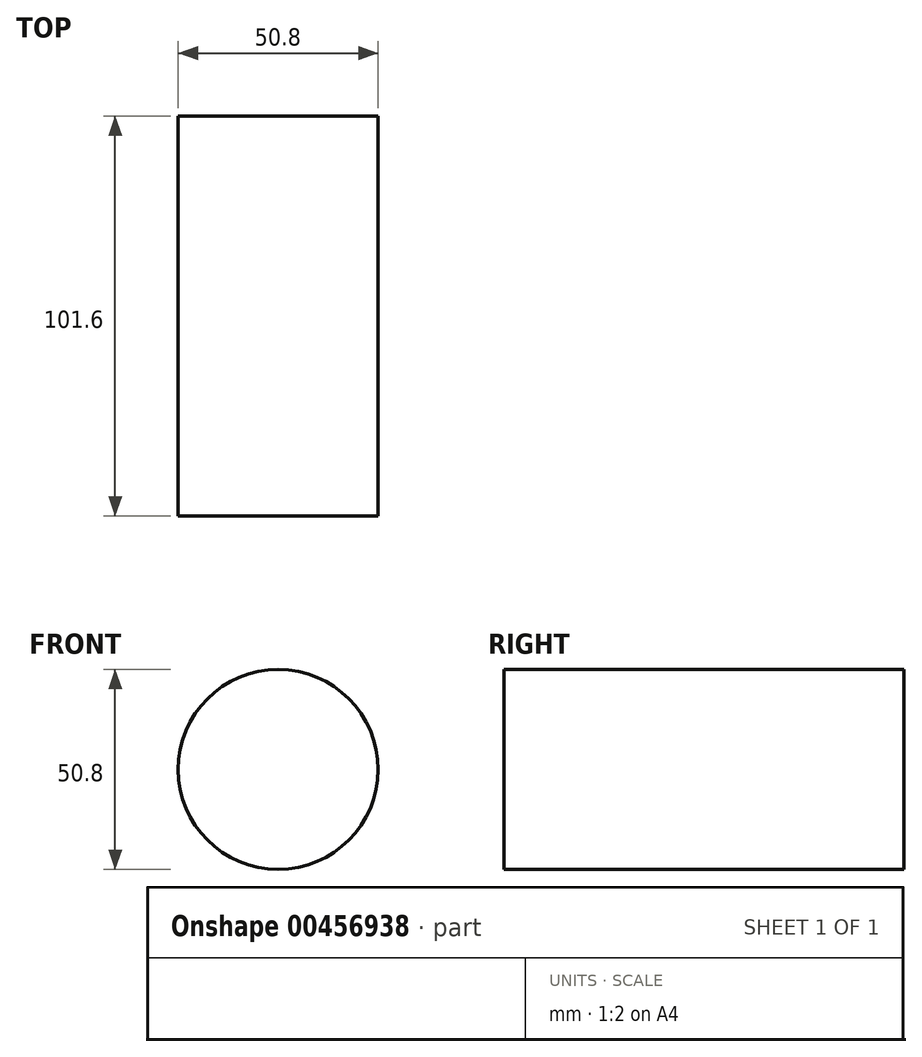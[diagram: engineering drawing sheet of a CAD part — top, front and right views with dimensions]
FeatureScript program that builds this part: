
annotation { "Feature Type Name" : "Feature", "Feature Type Description" : "" }
export const myFeature = defineFeature(function(context is Context, id is Id, definition is map)
    precondition{}
    {
        {
            var Q0;
            Q0=qCreatedBy(makeId("Front.planeOp"),FACE);
            var sketch = newSketch(context, id + "F0", { "sketchPlane" : qUnion([Q0])});
            skCircle(sketch, "E0", {"center": v(0, 0) * mm, "radius": 25.4 * mm});
            skCircle(sketch, "E1", {"center": v(0, 0) * mm, "radius": 50.8 * mm});
            skCircle(sketch, "E2", {"center": v(-38.1, 0) * mm, "radius": 6.35 * mm});
            skCircle(sketch, "E3.1.0", {"center": v(19.05, -33) * mm, "radius": 6.35 * mm});
            skCircle(sketch, "E3.2.0", {"center": v(19.05, 33) * mm, "radius": 6.35 * mm});
            skSolve(sketch);
        }
        {
            var Q0;
            Q0=makeQuery(id+"F0.imprint","IMPRINT",FACE,{"disambiguationData":[TD([[makeQuery(id+"F0.imprint","IMPRINT",EDGE,{"derivedFrom":sQuery(id+"F0.wireOp",EDGE,"E0")}),1.0]])]});
            extrude(context, id + "F1", {"entities" : qUnion([Q0]), "depth" : 101.6 * mm});
        }
    });
